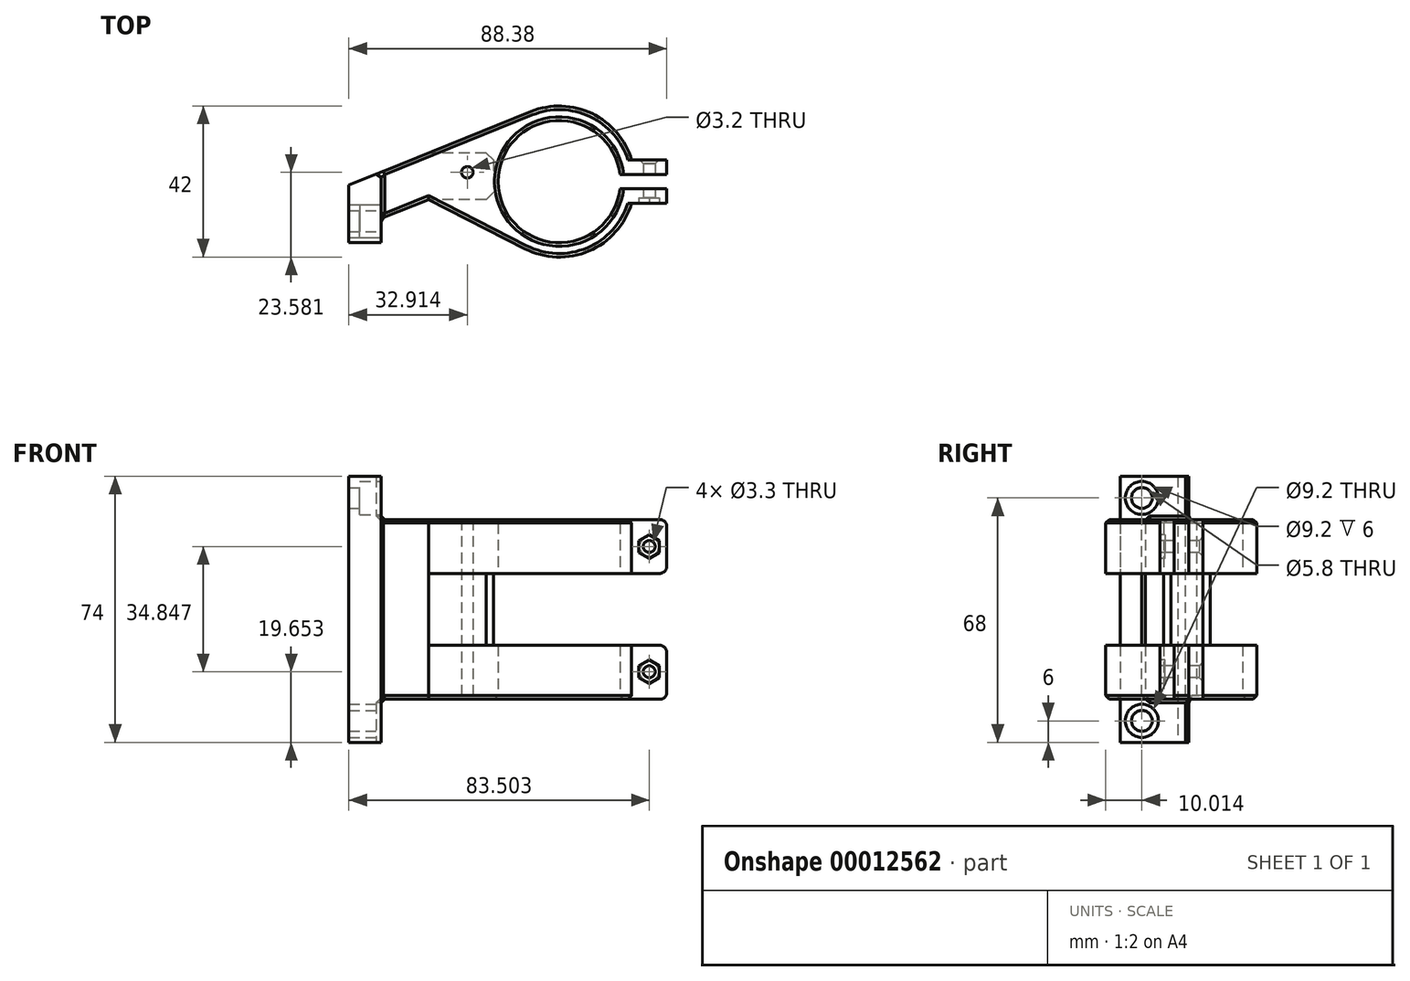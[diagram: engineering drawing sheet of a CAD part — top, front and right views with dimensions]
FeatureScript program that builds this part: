
annotation { "Feature Type Name" : "Feature", "Feature Type Description" : "" }
export const myFeature = defineFeature(function(context is Context, id is Id, definition is map)
    precondition{}
    {
        {
            var Q0;
            Q0=qCreatedBy(makeId("Top.planeOp"),FACE);
            var sketch = newSketch(context, id + "F0", { "sketchPlane" : qUnion([Q0])});
            skArc(sketch, "E0", {"start": v(20.12, 6) * mm, "mid": v(-21, 0) * mm, "end": v(20.12, -6) * mm});
            skLineSegment(sketch, "E1", {"start": v(-7.87, 19.47) * mm, "end": v(-58.5, -0.99) * mm});
            skLineSegment(sketch, "E2", {"start": v(-58.5, -0.99) * mm, "end": v(-58.5, -16.99) * mm});
            skLineSegment(sketch, "E3", {"start": v(-58.5, -16.99) * mm, "end": v(-49.5, -16.99) * mm});
            skLineSegment(sketch, "E4", {"start": v(-49.5, -10.3) * mm, "end": v(-36.32, -4.97) * mm});
            skLineSegment(sketch, "E5", {"start": v(-9.58, -18.69) * mm, "end": v(-36.32, -4.97) * mm});
            skLineSegment(sketch, "E6", {"start": v(-49.5, -16.99) * mm, "end": v(-49.5, -10.3) * mm});
            skCircle(sketch, "E7", {"center": v(-25.59, 2.58) * mm, "radius": 1.6 * mm});
            skArc(sketch, "E8.0", {"start": v(16.88, 2) * mm, "mid": v(-17, 0) * mm, "end": v(16.88, -2) * mm});
            skLineSegment(sketch, "E9", {"start": v(0, 0) * mm, "end": v(37.75, 0) * mm, "construction": true});
            skLineSegment(sketch, "E10.bottom", {"start": v(16.88, 2) * mm, "end": v(29.88, 2) * mm});
            skLineSegment(sketch, "E10.top", {"start": v(16.88, -2) * mm, "end": v(29.88, -2) * mm});
            skLineSegment(sketch, "E11.0", {"start": v(20.12, -6) * mm, "end": v(29.88, -6) * mm});
            skLineSegment(sketch, "E11.2", {"start": v(20.12, 6) * mm, "end": v(29.88, 6) * mm});
            skLineSegment(sketch, "E12", {"start": v(29.88, 2) * mm, "end": v(29.88, 6) * mm});
            skLineSegment(sketch, "E13", {"start": v(29.88, -2) * mm, "end": v(29.88, -6) * mm});
            skSolve(sketch);
        }
        {
            var Q0;
            {var subQ0=sQuery(id+"F0.wireOp",EDGE,"E5");var subQ1=sQuery(id+"F0.wireOp",EDGE,"E0");var subQ3=makeQuery(id+"F0.imprint","INTERSECT",VERTEX,{"disambiguationData":[OD(0.0)],"derivedFrom":[subQ1,subQ0]});Q0=makeQuery(id+"F0.imprint","IMPRINT",FACE,{"disambiguationData":[TD([[makeQuery(id+"F0.imprint","IMPRINT",EDGE,{"disambiguationData":[TD([[subQ3,1.0]])],"derivedFrom":subQ1}),1.0]])]});}
            var Q1;
            Q1=makeQuery(id+"F0.imprint","IMPRINT",FACE,{"disambiguationData":[TD([[makeQuery(id+"F0.imprint","IMPRINT",EDGE,{"derivedFrom":sQuery(id+"F0.wireOp",EDGE,"E8.0")}),-1.0]])]});
            var Q2;
            {var subQ4=sQuery(id+"F0.wireOp",EDGE,"E1");Q2=makeQuery(id+"F0.imprint","IMPRINT",FACE,{"disambiguationData":[TD([[makeQuery(id+"F0.imprint","IMPRINT",EDGE,{"derivedFrom":subQ4}),1.0]])]});}
            extrude(context, id + "F1", {"entities" : qUnion([Q0, Q1, Q2]), "depth" : 74 * mm});
        }
        {
            var Q0;
            Q0=makeQuery(id+"F1.opExtrude","SWEPT_FACE",FACE,{"disambiguationData":[OSD([sQuery(id+"F0.wireOp",EDGE,"E3")])]});
            cPlane(context, id + "F2", {"entities" : qUnion([Q0]), "cplaneType" : CPlaneType.OFFSET, "offset" : 5 * mm, "width" : 150 * mm, "height" : 150 * mm});
        }
        {
            var Q0;
            Q0=qCreatedBy(id+"F2.planeOp",FACE);
            var sketch = newSketch(context, id + "F3", { "sketchPlane" : qUnion([Q0])});
            skLineSegment(sketch, "E14.bottom", {"start": v(-49.5, 74) * mm, "end": v(38.3, 74) * mm});
            skLineSegment(sketch, "E14.top", {"start": v(-49.5, 62) * mm, "end": v(38.3, 62) * mm});
            skLineSegment(sketch, "E14.left", {"start": v(-49.5, 74) * mm, "end": v(-49.5, 62) * mm});
            skLineSegment(sketch, "E14.right", {"start": v(38.3, 74) * mm, "end": v(38.3, 62) * mm});
            skLineSegment(sketch, "E15.bottom", {"start": v(-49.5, 0) * mm, "end": v(36.46, 0) * mm});
            skLineSegment(sketch, "E15.top", {"start": v(-49.5, 12) * mm, "end": v(36.46, 12) * mm});
            skLineSegment(sketch, "E15.left", {"start": v(-49.5, 0) * mm, "end": v(-49.5, 12) * mm});
            skLineSegment(sketch, "E15.right", {"start": v(36.46, 0) * mm, "end": v(36.46, 12) * mm});
            skLineSegment(sketch, "E16", {"start": v(-49.5, 37) * mm, "end": v(48.22, 37) * mm, "construction": true});
            skLineSegment(sketch, "E17.bottom", {"start": v(-36.32, 47) * mm, "end": v(38.3, 47) * mm});
            skLineSegment(sketch, "E17.top", {"start": v(-36.32, 27) * mm, "end": v(38.3, 27) * mm});
            skLineSegment(sketch, "E17.left", {"start": v(-36.32, 47) * mm, "end": v(-36.32, 27) * mm});
            skLineSegment(sketch, "E17.right", {"start": v(38.3, 47) * mm, "end": v(38.3, 27) * mm});
            skSolve(sketch);
        }
        {
            var Q0;
            Q0=qSketchRegion(id+"F3",true);
            extrude(context, id + "F4", {"entities" : qUnion([Q0]), "operationType" : NewBodyOperationType.REMOVE, "endBound" : BoundingType.THROUGH_ALL, "oppositeDirection" : true, "depth" : 25 * mm});
        }
        {
            var Q0;
            Q0=makeQuery(id+"F4.boolean.opBoolean","MERGE",FACE,{"derivedFrom":[makeQuery(id+"F1.opExtrude","SWEPT_FACE",FACE,{"disambiguationData":[OSD([sQuery(id+"F0.wireOp",EDGE,"E6")])]}),makeQuery(id+"F4.opExtrude","SWEPT_FACE",FACE,{"disambiguationData":[OSD([sQuery(id+"F3.wireOp",EDGE,"E14.left")])]}),makeQuery(id+"F4.opExtrude","SWEPT_FACE",FACE,{"disambiguationData":[OSD([sQuery(id+"F3.wireOp",EDGE,"E15.left")])]})]});
            var sketch = newSketch(context, id + "F5", { "sketchPlane" : qUnion([Q0])});
            skCircle(sketch, "E18", {"center": v(-10.99, 68) * mm, "radius": 4.6 * mm});
            skCircle(sketch, "E19", {"center": v(-10.99, 68) * mm, "radius": 2.9 * mm});
            skLineSegment(sketch, "E20", {"start": v(-16.99, 37) * mm, "end": v(-52.07, 37) * mm, "construction": true});
            skCircle(sketch, "E21.0.MirrorC", {"center": v(-10.99, 6) * mm, "radius": 4.6 * mm});
            skCircle(sketch, "E21.1.MirrorC", {"center": v(-10.99, 6) * mm, "radius": 2.9 * mm});
            skSolve(sketch);
        }
        {
            var Q0;
            Q0=qSketchRegion(id+"F5",true);
            var Q1;
            Q1=makeQuery(id+"F5.imprint","IMPRINT",FACE,{"disambiguationData":[TD([[makeQuery(id+"F5.imprint","IMPRINT",EDGE,{"derivedFrom":sQuery(id+"F5.wireOp",EDGE,"E21.1.MirrorC")}),-1.0]])]});
            var Q2;
            Q2=makeQuery(id+"F5.imprint","IMPRINT",FACE,{"disambiguationData":[TD([[makeQuery(id+"F5.imprint","IMPRINT",EDGE,{"derivedFrom":sQuery(id+"F5.wireOp",EDGE,"E19")}),1.0]])]});
            extrude(context, id + "F6", {"entities" : qUnion([Q0, Q1, Q2]), "operationType" : NewBodyOperationType.REMOVE, "oppositeDirection" : true, "depth" : 6 * mm});
        }
        {
            var Q0;
            Q0=makeQuery(id+"F5.imprint","IMPRINT",FACE,{"disambiguationData":[TD([[makeQuery(id+"F5.imprint","IMPRINT",EDGE,{"derivedFrom":sQuery(id+"F5.wireOp",EDGE,"E19")}),1.0]])]});
            var Q1;
            Q1=makeQuery(id+"F5.imprint","IMPRINT",FACE,{"disambiguationData":[TD([[makeQuery(id+"F5.imprint","IMPRINT",EDGE,{"derivedFrom":sQuery(id+"F5.wireOp",EDGE,"E21.1.MirrorC")}),-1.0]])]});
            extrude(context, id + "F7", {"entities" : qUnion([Q0, Q1]), "operationType" : NewBodyOperationType.REMOVE, "endBound" : BoundingType.THROUGH_ALL, "oppositeDirection" : true, "depth" : 25 * mm});
        }
        {
            var Q0;
            {var subQ0=sQuery(id+"F0.wireOp",EDGE,"E11.0");Q0=makeQuery(id+"F4.boolean.opBoolean","SPLIT",FACE,{"disambiguationData":[TD([makeQuery(id+"F4.opExtrude","SWEPT_FACE",FACE,{"disambiguationData":[OSD([sQuery(id+"F3.wireOp",EDGE,"E14.top")])]})])],"derivedFrom":makeQuery(id+"F1.opExtrude","SWEPT_FACE",FACE,{"disambiguationData":[OSD([subQ0])]})});}
            var sketch = newSketch(context, id + "F8", { "sketchPlane" : qUnion([Q0])});
            skLineSegment(sketch, "E22", {"start": v(25, 62) * mm, "end": v(25, 47) * mm, "construction": true});
            skLineSegment(sketch, "E23", {"start": v(29.88, 54.5) * mm, "end": v(20.12, 54.5) * mm, "construction": true});
            skCircle(sketch, "E24.cCircle", {"center": v(25, 54.5) * mm, "radius": 2.86 * mm, "construction": true});
            skLineSegment(sketch, "E24.0", {"start": v(27.86, 56.15) * mm, "end": v(27.86, 52.85) * mm});
            skLineSegment(sketch, "E24.1", {"start": v(27.86, 52.85) * mm, "end": v(25, 51.2) * mm});
            skLineSegment(sketch, "E24.2", {"start": v(25, 51.2) * mm, "end": v(22.15, 52.85) * mm});
            skLineSegment(sketch, "E24.3", {"start": v(22.15, 52.85) * mm, "end": v(22.15, 56.15) * mm});
            skLineSegment(sketch, "E24.4", {"start": v(22.15, 56.15) * mm, "end": v(25, 57.8) * mm});
            skLineSegment(sketch, "E24.5", {"start": v(25, 57.8) * mm, "end": v(27.86, 56.15) * mm});
            skPoint(sketch, "E24.0.midPoint", {"position": v(27.86, 54.5) * mm});
            skCircle(sketch, "E25", {"center": v(25, 54.5) * mm, "radius": 1.65 * mm});
            skLineSegment(sketch, "E26", {"start": v(29.88, 47) * mm, "end": v(29.88, 27.15) * mm, "construction": true});
            skLineSegment(sketch, "E27", {"start": v(29.88, 37.08) * mm, "end": v(-2.17, 37.08) * mm, "construction": true});
            skLineSegment(sketch, "E28.0.MirrorCS", {"start": v(27.86, 18) * mm, "end": v(27.86, 21.3) * mm});
            skLineSegment(sketch, "E28.1.MirrorCS", {"start": v(25, 22.95) * mm, "end": v(22.15, 21.3) * mm});
            skCircle(sketch, "E28.2.MirrorC", {"center": v(25, 19.65) * mm, "radius": 1.65 * mm});
            skLineSegment(sketch, "E28.3.MirrorCS", {"start": v(27.86, 21.3) * mm, "end": v(25, 22.95) * mm});
            skPoint(sketch, "E28.4.MirrorP", {"position": v(27.86, 19.65) * mm});
            skLineSegment(sketch, "E28.5.MirrorCS", {"start": v(29.88, 19.65) * mm, "end": v(20.12, 19.65) * mm, "construction": true});
            skLineSegment(sketch, "E28.6.MirrorCS", {"start": v(25, 12.15) * mm, "end": v(25, 27.15) * mm, "construction": true});
            skLineSegment(sketch, "E28.7.MirrorCS", {"start": v(22.15, 21.3) * mm, "end": v(22.15, 18) * mm});
            skLineSegment(sketch, "E28.8.MirrorCS", {"start": v(25, 16.35) * mm, "end": v(27.86, 18) * mm});
            skCircle(sketch, "E28.9.MirrorC", {"center": v(25, 19.65) * mm, "radius": 2.86 * mm, "construction": true});
            skLineSegment(sketch, "E28.10.MirrorCS", {"start": v(22.15, 18) * mm, "end": v(25, 16.35) * mm});
            skSolve(sketch);
        }
        {
            var Q0;
            Q0=makeQuery(id+"F8.imprint","IMPRINT",FACE,{"disambiguationData":[TD([[makeQuery(id+"F8.imprint","IMPRINT",EDGE,{"derivedFrom":sQuery(id+"F8.wireOp",EDGE,"E24.0")}),-1.0]])]});
            var Q1;
            Q1=makeQuery(id+"F8.imprint","IMPRINT",FACE,{"disambiguationData":[TD([[makeQuery(id+"F8.imprint","IMPRINT",EDGE,{"derivedFrom":sQuery(id+"F8.wireOp",EDGE,"E28.0.MirrorCS")}),1.0]])]});
            extrude(context, id + "F9", {"entities" : qUnion([Q0, Q1]), "operationType" : NewBodyOperationType.REMOVE, "oppositeDirection" : true, "depth" : 1.5 * mm});
        }
        {
            var Q0;
            {var subQ0=sQuery(id+"F0.wireOp",EDGE,"E11.0");Q0=makeQuery(id+"F9.boolean.opBoolean","SPLIT",FACE,{"disambiguationData":[TD([makeQuery(id+"F9.opExtrude","SWEPT_FACE",FACE,{"disambiguationData":[OSD([sQuery(id+"F8.wireOp",EDGE,"E28.2.MirrorC")])]})])],"derivedFrom":makeQuery(id+"F4.boolean.opBoolean","SPLIT",FACE,{"disambiguationData":[TD([makeQuery(id+"F4.opExtrude","SWEPT_FACE",FACE,{"disambiguationData":[OSD([sQuery(id+"F3.wireOp",EDGE,"E15.top")])]})])],"derivedFrom":makeQuery(id+"F1.opExtrude","SWEPT_FACE",FACE,{"disambiguationData":[OSD([subQ0])]})})});}
            var Q1;
            {var subQ0=sQuery(id+"F0.wireOp",EDGE,"E11.0");Q1=makeQuery(id+"F9.boolean.opBoolean","SPLIT",FACE,{"disambiguationData":[TD([makeQuery(id+"F9.opExtrude","SWEPT_FACE",FACE,{"disambiguationData":[OSD([sQuery(id+"F8.wireOp",EDGE,"E25")])]})])],"derivedFrom":makeQuery(id+"F4.boolean.opBoolean","SPLIT",FACE,{"disambiguationData":[TD([makeQuery(id+"F4.opExtrude","SWEPT_FACE",FACE,{"disambiguationData":[OSD([sQuery(id+"F3.wireOp",EDGE,"E14.top")])]})])],"derivedFrom":makeQuery(id+"F1.opExtrude","SWEPT_FACE",FACE,{"disambiguationData":[OSD([subQ0])]})})});}
            extrude(context, id + "F10", {"entities" : qUnion([Q0, Q1]), "operationType" : NewBodyOperationType.REMOVE, "endBound" : BoundingType.THROUGH_ALL, "oppositeDirection" : true, "depth" : 25 * mm});
        }
        {
            var Q0;
            {var subQ0=sQuery(id+"F0.wireOp",EDGE,"E11.2");Q0=makeQuery(id+"F10.boolean.opBoolean","INTERSECT",EDGE,{"derivedFrom":[makeQuery(id+"F4.boolean.opBoolean","SPLIT",FACE,{"disambiguationData":[TD([makeQuery(id+"F4.opExtrude","SWEPT_FACE",FACE,{"disambiguationData":[OSD([sQuery(id+"F3.wireOp",EDGE,"E14.top")])]})])],"derivedFrom":makeQuery(id+"F1.opExtrude","SWEPT_FACE",FACE,{"disambiguationData":[OSD([subQ0])]})}),makeQuery(id+"F10.opExtrude","SWEPT_FACE",FACE,{"disambiguationData":[OSD([sQuery(id+"F8.wireOp",EDGE,"E25")])]})]});}
            var Q1;
            {var subQ0=sQuery(id+"F0.wireOp",EDGE,"E11.2");Q1=makeQuery(id+"F10.boolean.opBoolean","INTERSECT",EDGE,{"derivedFrom":[makeQuery(id+"F4.boolean.opBoolean","SPLIT",FACE,{"disambiguationData":[TD([makeQuery(id+"F4.opExtrude","SWEPT_FACE",FACE,{"disambiguationData":[OSD([sQuery(id+"F3.wireOp",EDGE,"E15.top")])]})])],"derivedFrom":makeQuery(id+"F1.opExtrude","SWEPT_FACE",FACE,{"disambiguationData":[OSD([subQ0])]})}),makeQuery(id+"F10.opExtrude","SWEPT_FACE",FACE,{"disambiguationData":[OSD([sQuery(id+"F8.wireOp",EDGE,"E28.2.MirrorC")])]})]});}
            chamfer(context, id + "F11", {"entities" : qUnion([Q0, Q1]), "width" : 1 * mm, "tangentPropagation" : true});
        }
        {
            var Q0;
            Q0=makeQuery(id+"F4.boolean.opBoolean","INTERSECT",EDGE,{"derivedFrom":[makeQuery(id+"F1.opExtrude","SWEPT_FACE",FACE,{"disambiguationData":[OSD([sQuery(id+"F0.wireOp",EDGE,"E8.0")])]}),makeQuery(id+"F4.opExtrude","SWEPT_FACE",FACE,{"disambiguationData":[OSD([sQuery(id+"F3.wireOp",EDGE,"E14.top")])]})]});
            var Q1;
            Q1=makeQuery(id+"F4.boolean.opBoolean","INTERSECT",EDGE,{"derivedFrom":[makeQuery(id+"F1.opExtrude","SWEPT_FACE",FACE,{"disambiguationData":[OSD([sQuery(id+"F0.wireOp",EDGE,"E8.0")])]}),makeQuery(id+"F4.opExtrude","SWEPT_FACE",FACE,{"disambiguationData":[OSD([sQuery(id+"F3.wireOp",EDGE,"E15.top")])]})]});
            chamfer(context, id + "F12", {"entities" : qUnion([Q0, Q1]), "width" : 1 * mm, "tangentPropagation" : true});
        }
        {
            var Q0;
            Q0=makeQuery(id+"F4.boolean.opBoolean","INTERSECT",EDGE,{"derivedFrom":[makeQuery(id+"F1.opExtrude","SWEPT_FACE",FACE,{"disambiguationData":[OSD([sQuery(id+"F0.wireOp",EDGE,"E12")])]}),makeQuery(id+"F4.opExtrude","SWEPT_FACE",FACE,{"disambiguationData":[OSD([sQuery(id+"F3.wireOp",EDGE,"E14.top")])]})]});
            var Q1;
            Q1=makeQuery(id+"F4.boolean.opBoolean","INTERSECT",EDGE,{"derivedFrom":[makeQuery(id+"F1.opExtrude","SWEPT_FACE",FACE,{"disambiguationData":[OSD([sQuery(id+"F0.wireOp",EDGE,"E13")])]}),makeQuery(id+"F4.opExtrude","SWEPT_FACE",FACE,{"disambiguationData":[OSD([sQuery(id+"F3.wireOp",EDGE,"E14.top")])]})]});
            var Q2;
            Q2=makeQuery(id+"F4.boolean.opBoolean","INTERSECT",EDGE,{"derivedFrom":[makeQuery(id+"F1.opExtrude","SWEPT_FACE",FACE,{"disambiguationData":[OSD([sQuery(id+"F0.wireOp",EDGE,"E13")])]}),makeQuery(id+"F4.opExtrude","SWEPT_FACE",FACE,{"disambiguationData":[OSD([sQuery(id+"F3.wireOp",EDGE,"E17.bottom")])]})]});
            var Q3;
            Q3=makeQuery(id+"F4.boolean.opBoolean","INTERSECT",EDGE,{"derivedFrom":[makeQuery(id+"F1.opExtrude","SWEPT_FACE",FACE,{"disambiguationData":[OSD([sQuery(id+"F0.wireOp",EDGE,"E12")])]}),makeQuery(id+"F4.opExtrude","SWEPT_FACE",FACE,{"disambiguationData":[OSD([sQuery(id+"F3.wireOp",EDGE,"E17.bottom")])]})]});
            var Q4;
            Q4=makeQuery(id+"F4.boolean.opBoolean","INTERSECT",EDGE,{"derivedFrom":[makeQuery(id+"F1.opExtrude","SWEPT_FACE",FACE,{"disambiguationData":[OSD([sQuery(id+"F0.wireOp",EDGE,"E13")])]}),makeQuery(id+"F4.opExtrude","SWEPT_FACE",FACE,{"disambiguationData":[OSD([sQuery(id+"F3.wireOp",EDGE,"E17.top")])]})]});
            var Q5;
            Q5=makeQuery(id+"F4.boolean.opBoolean","INTERSECT",EDGE,{"derivedFrom":[makeQuery(id+"F1.opExtrude","SWEPT_FACE",FACE,{"disambiguationData":[OSD([sQuery(id+"F0.wireOp",EDGE,"E12")])]}),makeQuery(id+"F4.opExtrude","SWEPT_FACE",FACE,{"disambiguationData":[OSD([sQuery(id+"F3.wireOp",EDGE,"E17.top")])]})]});
            var Q6;
            Q6=makeQuery(id+"F4.boolean.opBoolean","INTERSECT",EDGE,{"derivedFrom":[makeQuery(id+"F1.opExtrude","SWEPT_FACE",FACE,{"disambiguationData":[OSD([sQuery(id+"F0.wireOp",EDGE,"E12")])]}),makeQuery(id+"F4.opExtrude","SWEPT_FACE",FACE,{"disambiguationData":[OSD([sQuery(id+"F3.wireOp",EDGE,"E15.top")])]})]});
            var Q7;
            Q7=makeQuery(id+"F4.boolean.opBoolean","INTERSECT",EDGE,{"derivedFrom":[makeQuery(id+"F1.opExtrude","SWEPT_FACE",FACE,{"disambiguationData":[OSD([sQuery(id+"F0.wireOp",EDGE,"E13")])]}),makeQuery(id+"F4.opExtrude","SWEPT_FACE",FACE,{"disambiguationData":[OSD([sQuery(id+"F3.wireOp",EDGE,"E15.top")])]})]});
            fillet(context, id + "F13", {"entities" : qUnion([Q0, Q1, Q2, Q3, Q4, Q5, Q6, Q7]), "radius" : 2 * mm, "tangentPropagation" : true, "allowEdgeOverflow" : false});
        }
        {
            var Q0;
            Q0=makeQuery(id+"F4.boolean.opBoolean","MERGE",EDGE,{"derivedFrom":[makeQuery(id+"F1.opExtrude","CAP_EDGE",EDGE,{"disambiguationData":[OSD([sQuery(id+"F0.wireOp",EDGE,"E6")])],"isStart":false}),makeQuery(id+"F4.opExtrude","SWEPT_EDGE",EDGE,{"disambiguationData":[OSD([sQuery(id+"F0.wireOp",EDGE,"E3"),sQuery(id+"F3.wireOp",EDGE,"E14.bottom"),sQuery(id+"F3.wireOp",EDGE,"E14.left")])]})]});
            var Q1;
            Q1=makeQuery(id+"F4.boolean.opBoolean","INTERSECT",EDGE,{"derivedFrom":[makeQuery(id+"F1.opExtrude","SWEPT_FACE",FACE,{"disambiguationData":[OSD([sQuery(id+"F0.wireOp",EDGE,"E1")])]}),makeQuery(id+"F4.opExtrude","SWEPT_FACE",FACE,{"disambiguationData":[OSD([sQuery(id+"F3.wireOp",EDGE,"E14.left")])]})]});
            var Q2;
            Q2=makeQuery(id+"F1.opExtrude","SWEPT_EDGE",EDGE,{"disambiguationData":[OSD([sQuery(id+"F0.wireOp",EDGE,"E3"),sQuery(id+"F0.wireOp",EDGE,"E6")])]});
            var Q3;
            Q3=makeQuery(id+"F4.boolean.opBoolean","MERGE",EDGE,{"derivedFrom":[makeQuery(id+"F1.opExtrude","CAP_EDGE",EDGE,{"disambiguationData":[OSD([sQuery(id+"F0.wireOp",EDGE,"E6")])],"isStart":true}),makeQuery(id+"F4.opExtrude","SWEPT_EDGE",EDGE,{"disambiguationData":[OSD([sQuery(id+"F0.wireOp",EDGE,"E3"),sQuery(id+"F3.wireOp",EDGE,"E15.bottom"),sQuery(id+"F3.wireOp",EDGE,"E15.left")])]})]});
            var Q4;
            Q4=makeQuery(id+"F4.boolean.opBoolean","INTERSECT",EDGE,{"derivedFrom":[makeQuery(id+"F1.opExtrude","SWEPT_FACE",FACE,{"disambiguationData":[OSD([sQuery(id+"F0.wireOp",EDGE,"E1")])]}),makeQuery(id+"F4.opExtrude","SWEPT_FACE",FACE,{"disambiguationData":[OSD([sQuery(id+"F3.wireOp",EDGE,"E15.left")])]})]});
            var Q5;
            Q5=makeQuery(id+"F1.opExtrude","SWEPT_EDGE",EDGE,{"disambiguationData":[OSD([sQuery(id+"F0.wireOp",EDGE,"E4"),sQuery(id+"F0.wireOp",EDGE,"E6")])]});
            var Q6;
            Q6=makeQuery(id+"F4.boolean.opBoolean","COPY",EDGE,{"derivedFrom":makeQuery(id+"F4.opExtrude","SWEPT_EDGE",EDGE,{"disambiguationData":[OSD([sQuery(id+"F0.wireOp",EDGE,"E3"),sQuery(id+"F0.wireOp",EDGE,"E6"),sQuery(id+"F3.wireOp",EDGE,"E14.top"),sQuery(id+"F3.wireOp",EDGE,"E14.left")])]})});
            var Q7;
            Q7=makeQuery(id+"F4.boolean.opBoolean","INTERSECT",EDGE,{"derivedFrom":[makeQuery(id+"F1.opExtrude","SWEPT_FACE",FACE,{"disambiguationData":[OSD([sQuery(id+"F0.wireOp",EDGE,"E4")])]}),makeQuery(id+"F4.opExtrude","SWEPT_FACE",FACE,{"disambiguationData":[OSD([sQuery(id+"F3.wireOp",EDGE,"E15.top")])]})]});
            var Q8;
            Q8=makeQuery(id+"F4.boolean.opBoolean","INTERSECT",EDGE,{"derivedFrom":[makeQuery(id+"F1.opExtrude","SWEPT_FACE",FACE,{"disambiguationData":[OSD([sQuery(id+"F0.wireOp",EDGE,"E5")])]}),makeQuery(id+"F4.opExtrude","SWEPT_FACE",FACE,{"disambiguationData":[OSD([sQuery(id+"F3.wireOp",EDGE,"E15.top")])]})]});
            var Q9;
            {var subQ0=sQuery(id+"F0.wireOp",EDGE,"E0");Q9=makeQuery(id+"F4.boolean.opBoolean","INTERSECT",EDGE,{"derivedFrom":[makeQuery(id+"F1.opExtrude","SWEPT_FACE",FACE,{"disambiguationData":[OSD([subQ0]),TDD([makeQuery(id+"F0.imprint","IMPRINT",EDGE,{"disambiguationData":[TD([[makeQuery(id+"F0.imprint","INTERSECT",VERTEX,{"derivedFrom":[subQ0,sQuery(id+"F0.wireOp",EDGE,"E11.0")]}),1.0]])],"derivedFrom":subQ0})])]}),makeQuery(id+"F4.opExtrude","SWEPT_FACE",FACE,{"disambiguationData":[OSD([sQuery(id+"F3.wireOp",EDGE,"E15.top")])]})]});}
            var Q10;
            Q10=makeQuery(id+"F4.boolean.opBoolean","INTERSECT",EDGE,{"derivedFrom":[makeQuery(id+"F1.opExtrude","SWEPT_FACE",FACE,{"disambiguationData":[OSD([sQuery(id+"F0.wireOp",EDGE,"E5")])]}),makeQuery(id+"F4.opExtrude","SWEPT_FACE",FACE,{"disambiguationData":[OSD([sQuery(id+"F3.wireOp",EDGE,"E14.top")])]})]});
            var Q11;
            {var subQ0=sQuery(id+"F0.wireOp",EDGE,"E0");Q11=makeQuery(id+"F4.boolean.opBoolean","INTERSECT",EDGE,{"derivedFrom":[makeQuery(id+"F1.opExtrude","SWEPT_FACE",FACE,{"disambiguationData":[OSD([subQ0]),TDD([makeQuery(id+"F0.imprint","IMPRINT",EDGE,{"disambiguationData":[TD([[makeQuery(id+"F0.imprint","INTERSECT",VERTEX,{"derivedFrom":[subQ0,sQuery(id+"F0.wireOp",EDGE,"E11.0")]}),1.0]])],"derivedFrom":subQ0})])]}),makeQuery(id+"F4.opExtrude","SWEPT_FACE",FACE,{"disambiguationData":[OSD([sQuery(id+"F3.wireOp",EDGE,"E14.top")])]})]});}
            var Q12;
            Q12=makeQuery(id+"F4.boolean.opBoolean","INTERSECT",EDGE,{"derivedFrom":[makeQuery(id+"F1.opExtrude","SWEPT_FACE",FACE,{"disambiguationData":[OSD([sQuery(id+"F0.wireOp",EDGE,"E4")])]}),makeQuery(id+"F4.opExtrude","SWEPT_FACE",FACE,{"disambiguationData":[OSD([sQuery(id+"F3.wireOp",EDGE,"E14.top")])]})]});
            chamfer(context, id + "F14", {"entities" : qUnion([Q0, Q1, Q2, Q3, Q4, Q5, Q6, Q7, Q8, Q9, Q10, Q11, Q12]), "width" : 1 * mm, "tangentPropagation" : true});
        }
        {
            var Q0;
            Q0=makeQuery(id+"F4.boolean.opBoolean","COPY",FACE,{"derivedFrom":makeQuery(id+"F4.opExtrude","SWEPT_FACE",FACE,{"disambiguationData":[OSD([sQuery(id+"F3.wireOp",EDGE,"E17.left")])]})});
            extrude(context, id + "F15", {"entities" : qUnion([Q0]), "operationType" : NewBodyOperationType.ADD, "depth" : 18 * mm});
        }
        {
            var Q0;
            Q0=makeQuery(id+"F15.opExtrude","SWEPT_FACE",FACE,{"disambiguationData":[OSD([sQuery(id+"F3.wireOp",EDGE,"E17.bottom"),sQuery(id+"F3.wireOp",EDGE,"E17.left")])]});
            extrude(context, id + "F16", {"entities" : qUnion([Q0]), "operationType" : NewBodyOperationType.REMOVE, "endBound" : BoundingType.THROUGH_ALL, "oppositeDirection" : true, "depth" : 25 * mm});
        }
        {
            var Q0;
            Q0=makeQuery(id+"F15.opExtrude","CAP_EDGE",EDGE,{"disambiguationData":[OSD([sQuery(id+"F0.wireOp",EDGE,"E4"),sQuery(id+"F0.wireOp",EDGE,"E5")])],"isStart":false});
            var Q1;
            Q1=makeQuery(id+"F15.opExtrude","CAP_EDGE",EDGE,{"disambiguationData":[OSD([sQuery(id+"F0.wireOp",EDGE,"E1"),sQuery(id+"F3.wireOp",EDGE,"E17.left")])],"isStart":false});
            chamfer(context, id + "F17", {"entities" : qUnion([Q0, Q1]), "width" : 2 * mm, "tangentPropagation" : true});
        }
    });
